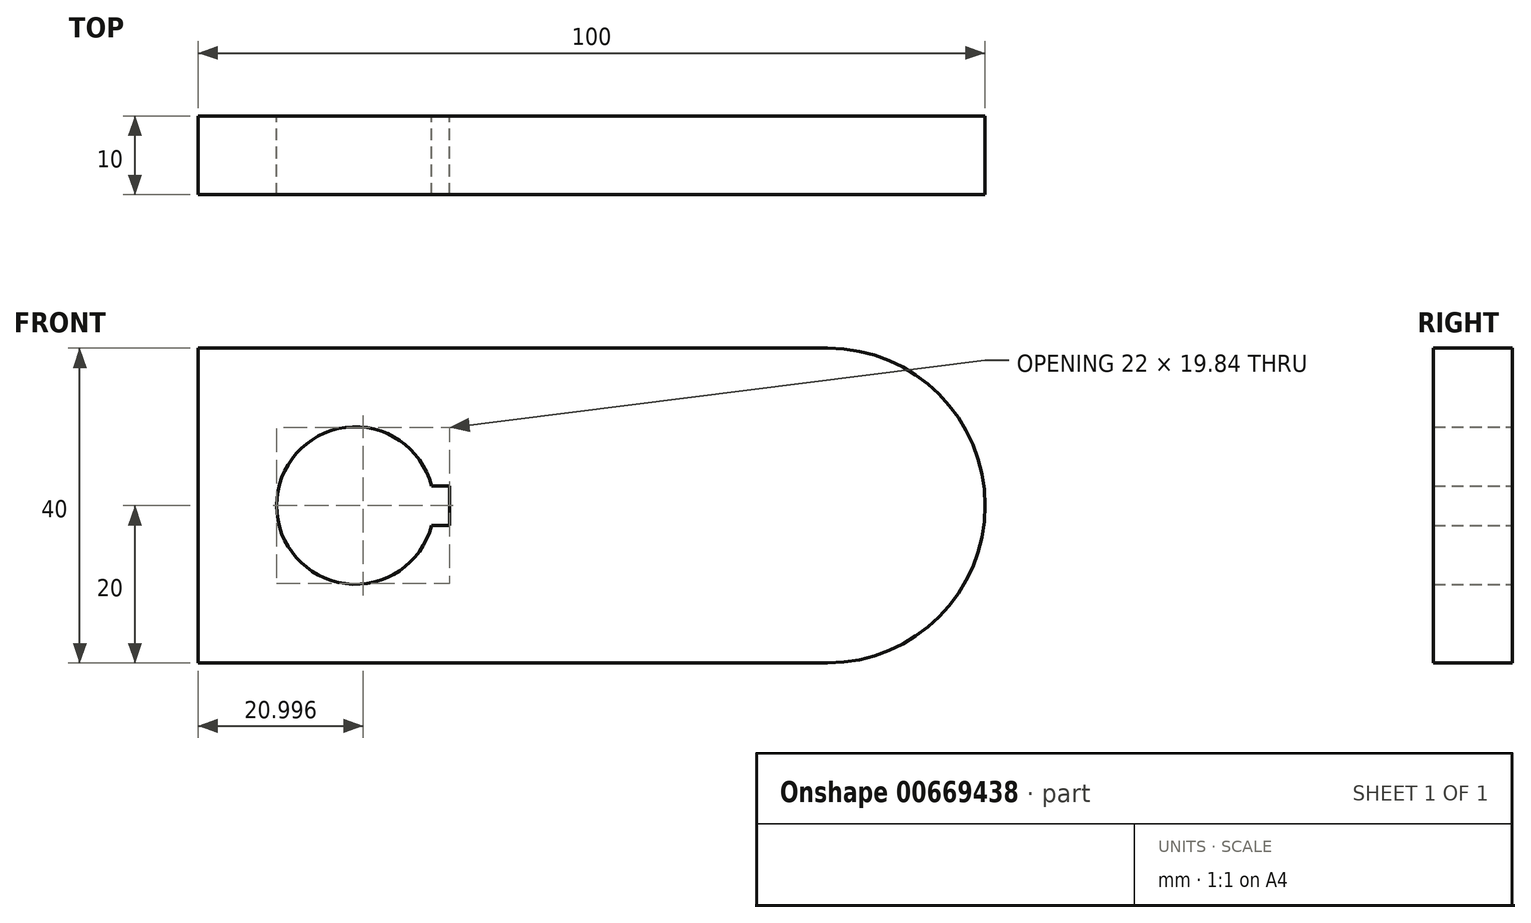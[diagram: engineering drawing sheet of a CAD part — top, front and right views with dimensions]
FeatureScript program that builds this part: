
annotation { "Feature Type Name" : "Feature", "Feature Type Description" : "" }
export const myFeature = defineFeature(function(context is Context, id is Id, definition is map)
    precondition{}
    {
        {
            var Q0;
            Q0=qCreatedBy(makeId("Front.planeOp"),FACE);
            var sketch = newSketch(context, id + "F0", { "sketchPlane" : qUnion([Q0])});
            skLineSegment(sketch, "E0.bottom", {"start": v(-43.64, 20) * mm, "end": v(36.36, 20) * mm});
            skLineSegment(sketch, "E0.top", {"start": v(-43.64, -20) * mm, "end": v(36.36, -20) * mm});
            skLineSegment(sketch, "E0.left", {"start": v(-43.64, 20) * mm, "end": v(-43.64, -20) * mm});
            skArc(sketch, "E1", {"start": v(-13.96, 2.5) * mm, "mid": v(-33.64, 0) * mm, "end": v(-13.96, -2.5) * mm});
            skLineSegment(sketch, "E2.bottom", {"start": v(-13.96, 2.5) * mm, "end": v(-11.64, 2.5) * mm});
            skLineSegment(sketch, "E2.top", {"start": v(-13.96, -2.5) * mm, "end": v(-11.64, -2.5) * mm});
            skLineSegment(sketch, "E2.right", {"start": v(-11.64, 2.5) * mm, "end": v(-11.64, -2.5) * mm});
            skArc(sketch, "E3", {"start": v(36.36, -20) * mm, "mid": v(56.36, 0) * mm, "end": v(36.36, 20) * mm});
            skSolve(sketch);
        }
        {
            var Q0;
            Q0 = qSketchRegion(id + "F0", true);
            extrude(context, id + "F1", {"entities" : qUnion([Q0]), "depth" : 10 * mm, "offsetDistance" : 25 * mm});
        }
    });
